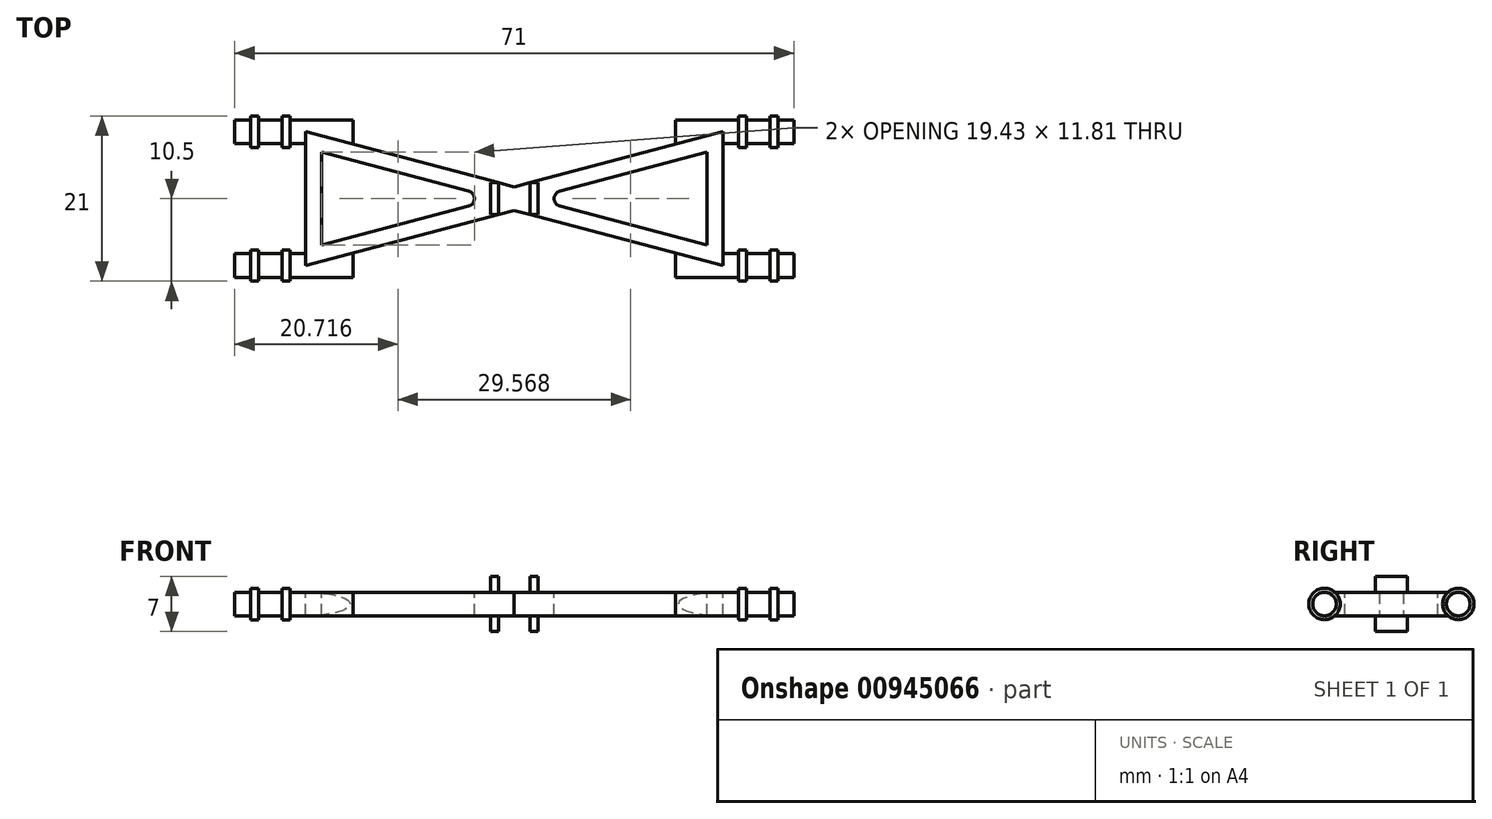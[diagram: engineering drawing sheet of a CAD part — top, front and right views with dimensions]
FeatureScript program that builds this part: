
annotation { "Feature Type Name" : "Feature", "Feature Type Description" : "" }
export const myFeature = defineFeature(function(context is Context, id is Id, definition is map)
    precondition{}
    {
        {
            var Q0;
            Q0=qCreatedBy(makeId("Top.planeOp"),FACE);
            var sketch = newSketch(context, id + "F0", { "sketchPlane" : qUnion([Q0])});
            skLineSegment(sketch, "E0", {"start": v(-26.5, 8.5) * mm, "end": v(-26.5, 0) * mm});
            skLineSegment(sketch, "E1", {"start": v(-26.5, 8.5) * mm, "end": v(0, 1.5) * mm});
            skLineSegment(sketch, "E2.MirrorCS", {"start": v(26.5, 8.5) * mm, "end": v(0, 1.5) * mm});
            skLineSegment(sketch, "E3.MirrorCS", {"start": v(26.5, 8.5) * mm, "end": v(26.5, 0) * mm});
            skLineSegment(sketch, "E4.MirrorCS", {"start": v(-26.5, -8.5) * mm, "end": v(-26.5, 0) * mm});
            skLineSegment(sketch, "E5.MirrorCS", {"start": v(-26.5, -8.5) * mm, "end": v(0, -1.5) * mm});
            skLineSegment(sketch, "E6.MirrorCS", {"start": v(26.5, -8.5) * mm, "end": v(0, -1.5) * mm});
            skLineSegment(sketch, "E7.MirrorCS", {"start": v(26.5, -8.5) * mm, "end": v(26.5, 0) * mm});
            skSolve(sketch);
        }
        {
            var Q0;
            Q0=makeQuery(id+"F0.imprint","IMPRINT",FACE,{"disambiguationData":[TD([[makeQuery(id+"F0.imprint","IMPRINT",EDGE,{"derivedFrom":sQuery(id+"F0.wireOp",EDGE,"2a235361-8aa0-4ffb-bb85-94337bc42d174.MirrorCS")}),1.0]])]});
            var Q1;
            Q1=makeQuery(id+"F0.imprint","IMPRINT",FACE,{"disambiguationData":[TD([[makeQuery(id+"F0.imprint","IMPRINT",EDGE,{"derivedFrom":sQuery(id+"F0.wireOp",EDGE,"E0")}),1.0]])]});
            extrude(context, id + "F1", {"entities" : qUnion([Q0, Q1]), "depth" : 3 * mm, "offsetDistance" : 25 * mm, "symmetric" : true});
        }
        {
            var Q0;
            Q0=makeQuery(id+"F1.opExtrude","CAP_FACE",FACE,{"disambiguationData":[OSD([sQuery(id+"F0.wireOp",EDGE,"E0"),sQuery(id+"F0.wireOp",EDGE,"E1"),sQuery(id+"F0.wireOp",EDGE,"E2.MirrorCS"),sQuery(id+"F0.wireOp",EDGE,"E3.MirrorCS"),sQuery(id+"F0.wireOp",EDGE,"E4.MirrorCS"),sQuery(id+"F0.wireOp",EDGE,"E5.MirrorCS"),sQuery(id+"F0.wireOp",EDGE,"E6.MirrorCS"),sQuery(id+"F0.wireOp",EDGE,"E7.MirrorCS")])],"isStart":false});
            var sketch = newSketch(context, id + "F2", { "sketchPlane" : qUnion([Q0])});
            skLineSegment(sketch, "E8", {"start": v(-24.5, 0) * mm, "end": v(-24.5, 5.9) * mm});
            skLineSegment(sketch, "E9", {"start": v(-24.5, 5.9) * mm, "end": v(-2.15, 0) * mm});
            skLineSegment(sketch, "E10.MirrorCS", {"start": v(24.5, 5.9) * mm, "end": v(2.15, 0) * mm});
            skLineSegment(sketch, "E11.MirrorCS", {"start": v(24.5, 0) * mm, "end": v(24.5, 5.9) * mm});
            skLineSegment(sketch, "E12.MirrorCS", {"start": v(-24.5, 0) * mm, "end": v(-24.5, -5.9) * mm});
            skLineSegment(sketch, "E13.MirrorCS", {"start": v(-24.5, -5.9) * mm, "end": v(-2.15, 0) * mm});
            skLineSegment(sketch, "E14.MirrorCS", {"start": v(24.5, -5.9) * mm, "end": v(2.15, 0) * mm});
            skLineSegment(sketch, "E15.MirrorCS", {"start": v(24.5, 0) * mm, "end": v(24.5, -5.9) * mm});
            skSolve(sketch);
        }
        {
            var Q0;
            Q0=makeQuery(id+"F2.imprint","IMPRINT",FACE,{"disambiguationData":[TD([[makeQuery(id+"F2.imprint","IMPRINT",EDGE,{"derivedFrom":sQuery(id+"F2.wireOp",EDGE,"E8")}),-1.0]])]});
            var Q1;
            Q1=makeQuery(id+"F2.imprint","IMPRINT",FACE,{"disambiguationData":[TD([[makeQuery(id+"F2.imprint","IMPRINT",EDGE,{"derivedFrom":sQuery(id+"F2.wireOp",EDGE,"E10.MirrorCS")}),1.0]])]});
            extrude(context, id + "F3", {"entities" : qUnion([Q0, Q1]), "operationType" : NewBodyOperationType.REMOVE, "endBound" : BoundingType.THROUGH_ALL, "oppositeDirection" : true, "depth" : 25 * mm, "offsetDistance" : 25 * mm});
        }
        {
            var Q0;
            Q0=makeQuery(id+"F3.boolean.opBoolean","COPY",EDGE,{"derivedFrom":makeQuery(id+"F3.opExtrude","SWEPT_EDGE",EDGE,{"disambiguationData":[OSD([sQuery(id+"F2.wireOp",EDGE,"E9"),sQuery(id+"F2.wireOp",EDGE,"E13.MirrorCS")])]})});
            var Q1;
            Q1=makeQuery(id+"F3.boolean.opBoolean","COPY",EDGE,{"derivedFrom":makeQuery(id+"F3.opExtrude","SWEPT_EDGE",EDGE,{"disambiguationData":[OSD([sQuery(id+"F2.wireOp",EDGE,"E10.MirrorCS"),sQuery(id+"F2.wireOp",EDGE,"E14.MirrorCS")])]})});
            fillet(context, id + "F4", {"entities" : qUnion([Q0, Q1]), "radius" : 1 * mm, "tangentPropagation" : true, "defaultsChanged" : false, "vertexSettings" : [], "allowEdgeOverflow" : false});
        }
        {
            var Q0;
            Q0=qCreatedBy(makeId("Top.planeOp"),FACE);
            var sketch = newSketch(context, id + "F5", { "sketchPlane" : qUnion([Q0])});
            skLineSegment(sketch, "E16", {"start": v(35.5, 8.5) * mm, "end": v(35.5, 10) * mm});
            skLineSegment(sketch, "E17", {"start": v(35.5, 10) * mm, "end": v(33.5, 10) * mm});
            skLineSegment(sketch, "E18", {"start": v(33.5, 10) * mm, "end": v(33.5, 10.5) * mm});
            skLineSegment(sketch, "E19", {"start": v(33.5, 10.5) * mm, "end": v(32.5, 10.5) * mm});
            skLineSegment(sketch, "E20", {"start": v(32.5, 10.5) * mm, "end": v(32.5, 10) * mm});
            skLineSegment(sketch, "E21", {"start": v(32.5, 10) * mm, "end": v(29.5, 10) * mm});
            skLineSegment(sketch, "E22", {"start": v(29.5, 10) * mm, "end": v(29.5, 10.5) * mm});
            skLineSegment(sketch, "E23", {"start": v(29.5, 10.5) * mm, "end": v(28.5, 10.5) * mm});
            skLineSegment(sketch, "E24", {"start": v(28.5, 10.5) * mm, "end": v(28.5, 10) * mm});
            skLineSegment(sketch, "E25", {"start": v(28.5, 10) * mm, "end": v(20.5, 10) * mm});
            skLineSegment(sketch, "E26", {"start": v(20.5, 10) * mm, "end": v(20.5, 8.5) * mm});
            skLineSegment(sketch, "E27", {"start": v(20.5, 8.5) * mm, "end": v(35.5, 8.5) * mm});
            skSolve(sketch);
        }
        {
            var Q0;
            Q0=makeQuery(id+"F5.imprint","IMPRINT",FACE,{"disambiguationData":[TD([[makeQuery(id+"F5.imprint","IMPRINT",EDGE,{"derivedFrom":sQuery(id+"F5.wireOp",EDGE,"E16")}),1.0]])]});
            var Q1;
            Q1=sQuery(id+"F5.wireOp",EDGE,"E27");
            revolve(context, id + "F6", {"operationType" : NewBodyOperationType.ADD, "surfaceOperationType" : NewSurfaceOperationType.NEW, "entities" : qUnion([Q0]), "axis" : qUnion([Q1]), "revolveType" : RevolveType.FULL});
        }
        {
            var Q0;
            Q0=qCreatedBy(makeId("Top.planeOp"),FACE);
            var sketch = newSketch(context, id + "F7", { "sketchPlane" : qUnion([Q0])});
            skLineSegment(sketch, "E28.bottom", {"start": v(-3, 2.03) * mm, "end": v(-2, 2.03) * mm});
            skLineSegment(sketch, "E28.top", {"start": v(-3, -2.03) * mm, "end": v(-2, -2.03) * mm});
            skLineSegment(sketch, "E28.left", {"start": v(-3, 2.03) * mm, "end": v(-3, -2.03) * mm});
            skLineSegment(sketch, "E28.right", {"start": v(-2, 2.03) * mm, "end": v(-2, -2.03) * mm});
            skSolve(sketch);
        }
        {
            var Q0;
            Q0 = qSketchRegion(id + "F7", true);
            extrude(context, id + "F8", {"entities" : qUnion([Q0]), "operationType" : NewBodyOperationType.ADD, "depth" : 7 * mm, "offsetDistance" : 25 * mm, "symmetric" : true});
        }
        {
            var Q0;
            Q0=makeQuery(id+"F1.opExtrude","SWEPT_BODY",BODY,{"disambiguationData":[OSD([sQuery(id+"F0.wireOp",EDGE,"E0"),sQuery(id+"F0.wireOp",EDGE,"E1"),sQuery(id+"F0.wireOp",EDGE,"E2.MirrorCS"),sQuery(id+"F0.wireOp",EDGE,"E3.MirrorCS"),sQuery(id+"F0.wireOp",EDGE,"E4.MirrorCS"),sQuery(id+"F0.wireOp",EDGE,"E5.MirrorCS"),sQuery(id+"F0.wireOp",EDGE,"E6.MirrorCS"),sQuery(id+"F0.wireOp",EDGE,"E7.MirrorCS")])]});
            var Q1;
            Q1=qCreatedBy(makeId("Right.planeOp"),FACE);
            mirror(context, id + "F9", {"operationType" : NewBodyOperationType.ADD, "entities" : qUnion([Q0]), "mirrorPlane" : qUnion([Q1])});
        }
        {
            var Q0;
            Q0=makeQuery(id+"F1.opExtrude","SWEPT_BODY",BODY,{"disambiguationData":[OSD([sQuery(id+"F0.wireOp",EDGE,"E0"),sQuery(id+"F0.wireOp",EDGE,"E1"),sQuery(id+"F0.wireOp",EDGE,"E2.MirrorCS"),sQuery(id+"F0.wireOp",EDGE,"E3.MirrorCS"),sQuery(id+"F0.wireOp",EDGE,"E4.MirrorCS"),sQuery(id+"F0.wireOp",EDGE,"E5.MirrorCS"),sQuery(id+"F0.wireOp",EDGE,"E6.MirrorCS"),sQuery(id+"F0.wireOp",EDGE,"E7.MirrorCS")])]});
            var Q1;
            Q1=qCreatedBy(makeId("Front.planeOp"),FACE);
            mirror(context, id + "F10", {"operationType" : NewBodyOperationType.ADD, "entities" : qUnion([Q0]), "mirrorPlane" : qUnion([Q1])});
        }
    });
